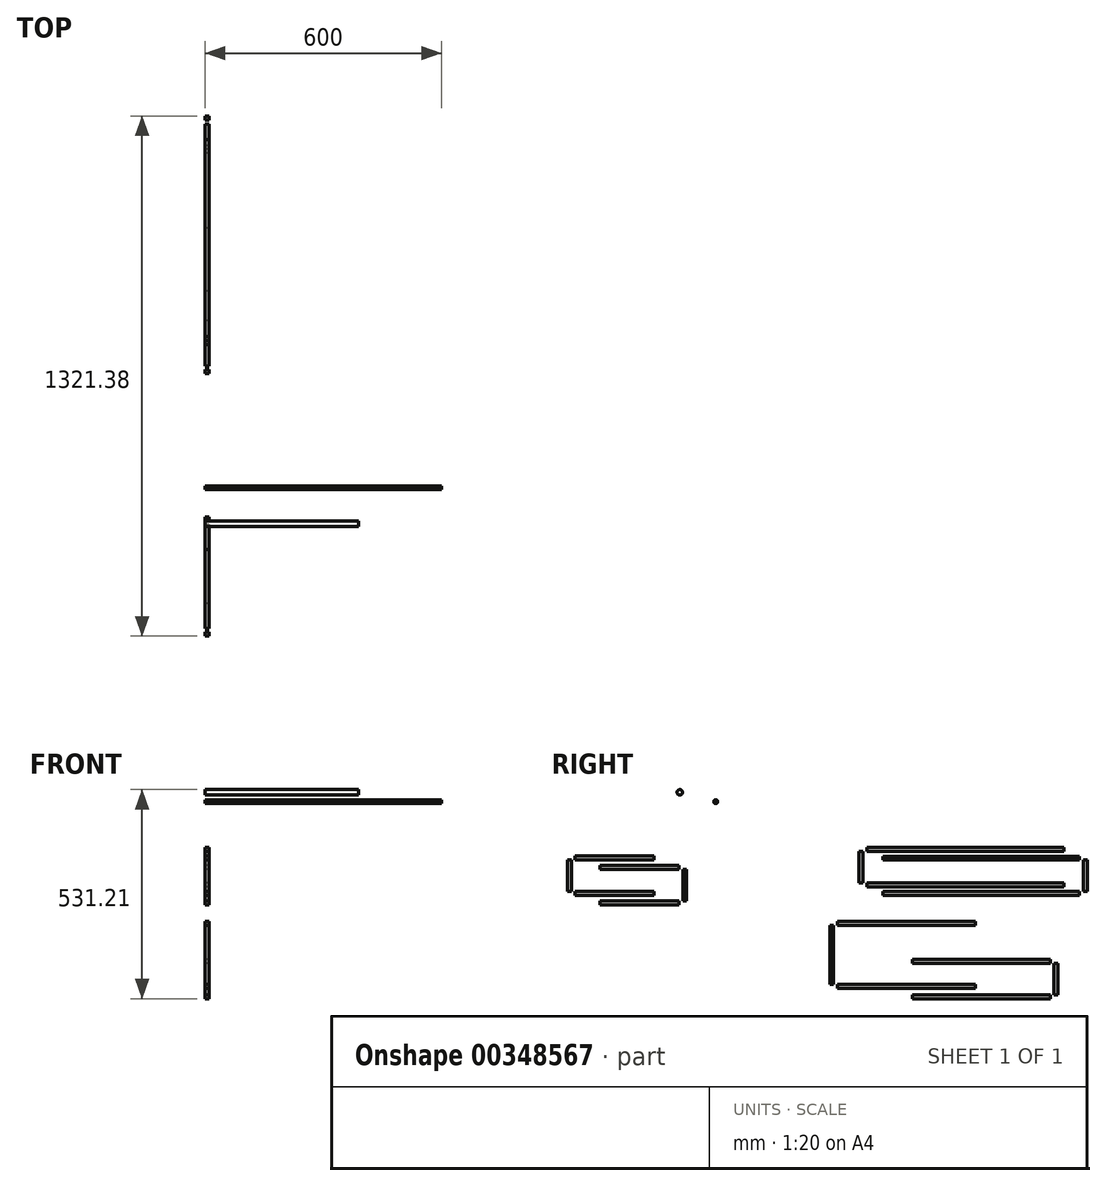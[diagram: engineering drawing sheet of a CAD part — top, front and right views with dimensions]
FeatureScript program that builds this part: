
annotation { "Feature Type Name" : "Feature", "Feature Type Description" : "" }
export const myFeature = defineFeature(function(context is Context, id is Id, definition is map)
    precondition{}
    {
        {
            var Q0;
            Q0=qCreatedBy(makeId("Right.planeOp"),FACE);
            var sketch = newSketch(context, id + "F0", { "sketchPlane" : qUnion([Q0])});
            skLineSegment(sketch, "E0.bottom", {"start": v(-89.52, 73.22) * mm, "end": v(-79.52, 73.22) * mm});
            skLineSegment(sketch, "E0.top", {"start": v(-89.52, -6.78) * mm, "end": v(-79.52, -6.78) * mm});
            skLineSegment(sketch, "E0.left", {"start": v(-89.52, 73.22) * mm, "end": v(-89.52, -6.78) * mm});
            skLineSegment(sketch, "E0.right", {"start": v(-79.52, 73.22) * mm, "end": v(-79.52, -6.78) * mm});
            skLineSegment(sketch, "E1.bottom", {"start": v(-69.52, 73.22) * mm, "end": v(430.48, 73.22) * mm});
            skLineSegment(sketch, "E1.top", {"start": v(-69.52, 83.22) * mm, "end": v(430.48, 83.22) * mm});
            skLineSegment(sketch, "E1.left", {"start": v(-69.52, 73.22) * mm, "end": v(-69.52, 83.22) * mm});
            skLineSegment(sketch, "E1.right", {"start": v(430.48, 73.22) * mm, "end": v(430.48, 83.22) * mm});
            skLineSegment(sketch, "E2.bottom", {"start": v(480.59, 50.91) * mm, "end": v(490.59, 50.91) * mm});
            skLineSegment(sketch, "E2.top", {"start": v(480.59, -29.09) * mm, "end": v(490.59, -29.09) * mm});
            skLineSegment(sketch, "E2.left", {"start": v(480.59, 50.91) * mm, "end": v(480.59, -29.09) * mm});
            skLineSegment(sketch, "E2.right", {"start": v(490.59, 50.91) * mm, "end": v(490.59, -29.09) * mm});
            skLineSegment(sketch, "E3.bottom", {"start": v(470.59, 50.91) * mm, "end": v(-29.41, 50.91) * mm});
            skLineSegment(sketch, "E3.top", {"start": v(470.59, 60.91) * mm, "end": v(-29.41, 60.91) * mm});
            skLineSegment(sketch, "E3.left", {"start": v(470.59, 50.91) * mm, "end": v(470.59, 60.91) * mm});
            skLineSegment(sketch, "E3.right", {"start": v(-29.41, 50.91) * mm, "end": v(-29.41, 60.91) * mm});
            skLineSegment(sketch, "E4.bottom", {"start": v(-69.52, -6.78) * mm, "end": v(430.48, -6.78) * mm});
            skLineSegment(sketch, "E4.top", {"start": v(-69.52, -16.78) * mm, "end": v(430.48, -16.78) * mm});
            skLineSegment(sketch, "E4.left", {"start": v(-69.52, -6.78) * mm, "end": v(-69.52, -16.78) * mm});
            skLineSegment(sketch, "E4.right", {"start": v(430.48, -6.78) * mm, "end": v(430.48, -16.78) * mm});
            skLineSegment(sketch, "E5.bottom", {"start": v(470.59, -29.09) * mm, "end": v(-29.41, -29.09) * mm});
            skLineSegment(sketch, "E5.top", {"start": v(470.59, -39.09) * mm, "end": v(-29.41, -39.09) * mm});
            skLineSegment(sketch, "E5.left", {"start": v(470.59, -29.09) * mm, "end": v(470.59, -39.09) * mm});
            skLineSegment(sketch, "E5.right", {"start": v(-29.41, -29.09) * mm, "end": v(-29.41, -39.09) * mm});
            skSolve(sketch);
        }
        {
            var Q0;
            Q0=qSketchRegion(id+"F0",true);
            extrude(context, id + "F1", {"entities" : qUnion([Q0]), "depth" : 10 * mm});
        }
        {
            var Q0;
            Q0=qCreatedBy(makeId("Right.planeOp"),FACE);
            var sketch = newSketch(context, id + "F2", { "sketchPlane" : qUnion([Q0])});
            skLineSegment(sketch, "E6.bottom", {"start": v(-164.15, -114.36) * mm, "end": v(-154.15, -114.36) * mm});
            skLineSegment(sketch, "E6.top", {"start": v(-164.15, -264.36) * mm, "end": v(-154.15, -264.36) * mm});
            skLineSegment(sketch, "E6.left", {"start": v(-164.15, -114.36) * mm, "end": v(-164.15, -264.36) * mm});
            skLineSegment(sketch, "E6.right", {"start": v(-154.15, -114.36) * mm, "end": v(-154.15, -264.36) * mm});
            skLineSegment(sketch, "E7.bottom", {"start": v(-144.15, -114.36) * mm, "end": v(205.85, -114.36) * mm});
            skLineSegment(sketch, "E7.top", {"start": v(-144.15, -104.36) * mm, "end": v(205.85, -104.36) * mm});
            skLineSegment(sketch, "E7.left", {"start": v(-144.15, -114.36) * mm, "end": v(-144.15, -104.36) * mm});
            skLineSegment(sketch, "E7.right", {"start": v(205.85, -114.36) * mm, "end": v(205.85, -104.36) * mm});
            skLineSegment(sketch, "E8.bottom", {"start": v(405.95, -211.05) * mm, "end": v(415.95, -211.05) * mm});
            skLineSegment(sketch, "E8.top", {"start": v(405.95, -291.05) * mm, "end": v(415.95, -291.05) * mm});
            skLineSegment(sketch, "E8.left", {"start": v(405.95, -211.05) * mm, "end": v(405.95, -291.05) * mm});
            skLineSegment(sketch, "E8.right", {"start": v(415.95, -211.05) * mm, "end": v(415.95, -291.05) * mm});
            skLineSegment(sketch, "E9.bottom", {"start": v(395.95, -211.05) * mm, "end": v(45.95, -211.05) * mm});
            skLineSegment(sketch, "E9.top", {"start": v(395.95, -201.05) * mm, "end": v(45.95, -201.05) * mm});
            skLineSegment(sketch, "E9.left", {"start": v(395.95, -211.05) * mm, "end": v(395.95, -201.05) * mm});
            skLineSegment(sketch, "E9.right", {"start": v(45.95, -211.05) * mm, "end": v(45.95, -201.05) * mm});
            skLineSegment(sketch, "E10.bottom", {"start": v(-144.15, -264.36) * mm, "end": v(205.85, -264.36) * mm});
            skLineSegment(sketch, "E10.top", {"start": v(-144.15, -274.36) * mm, "end": v(205.85, -274.36) * mm});
            skLineSegment(sketch, "E10.left", {"start": v(-144.15, -264.36) * mm, "end": v(-144.15, -274.36) * mm});
            skLineSegment(sketch, "E10.right", {"start": v(205.85, -264.36) * mm, "end": v(205.85, -274.36) * mm});
            skLineSegment(sketch, "E11.bottom", {"start": v(395.95, -291.05) * mm, "end": v(45.95, -291.05) * mm});
            skLineSegment(sketch, "E11.top", {"start": v(395.95, -301.05) * mm, "end": v(45.95, -301.05) * mm});
            skLineSegment(sketch, "E11.left", {"start": v(395.95, -291.05) * mm, "end": v(395.95, -301.05) * mm});
            skLineSegment(sketch, "E11.right", {"start": v(45.95, -291.05) * mm, "end": v(45.95, -301.05) * mm});
            skSolve(sketch);
        }
        {
            var Q0;
            Q0=qSketchRegion(id+"F2",true);
            extrude(context, id + "F3", {"entities" : qUnion([Q0]), "depth" : 10 * mm});
        }
        {
            var Q0;
            Q0=qCreatedBy(makeId("Right.planeOp"),FACE);
            var sketch = newSketch(context, id + "F4", { "sketchPlane" : qUnion([Q0])});
            skLineSegment(sketch, "E12.bottom", {"start": v(-830.8, 51.15) * mm, "end": v(-820.8, 51.15) * mm});
            skLineSegment(sketch, "E12.top", {"start": v(-830.8, -28.85) * mm, "end": v(-820.8, -28.85) * mm});
            skLineSegment(sketch, "E12.left", {"start": v(-830.8, 51.15) * mm, "end": v(-830.8, -28.85) * mm});
            skLineSegment(sketch, "E12.right", {"start": v(-820.8, 51.15) * mm, "end": v(-820.8, -28.85) * mm});
            skLineSegment(sketch, "E13.bottom", {"start": v(-810.8, 51.15) * mm, "end": v(-610.8, 51.15) * mm});
            skLineSegment(sketch, "E13.top", {"start": v(-810.8, 61.15) * mm, "end": v(-610.8, 61.15) * mm});
            skLineSegment(sketch, "E13.left", {"start": v(-810.8, 51.15) * mm, "end": v(-810.8, 61.15) * mm});
            skLineSegment(sketch, "E13.right", {"start": v(-610.8, 51.15) * mm, "end": v(-610.8, 61.15) * mm});
            skLineSegment(sketch, "E14.bottom", {"start": v(-537.58, 27) * mm, "end": v(-527.58, 27) * mm});
            skLineSegment(sketch, "E14.top", {"start": v(-537.58, -53) * mm, "end": v(-527.58, -53) * mm});
            skLineSegment(sketch, "E14.left", {"start": v(-537.58, 27) * mm, "end": v(-537.58, -53) * mm});
            skLineSegment(sketch, "E14.right", {"start": v(-527.58, 27) * mm, "end": v(-527.58, -53) * mm});
            skLineSegment(sketch, "E15.bottom", {"start": v(-547.58, 27) * mm, "end": v(-747.58, 27) * mm});
            skLineSegment(sketch, "E15.top", {"start": v(-547.58, 37) * mm, "end": v(-747.58, 37) * mm});
            skLineSegment(sketch, "E15.left", {"start": v(-547.58, 27) * mm, "end": v(-547.58, 37) * mm});
            skLineSegment(sketch, "E15.right", {"start": v(-747.58, 27) * mm, "end": v(-747.58, 37) * mm});
            skLineSegment(sketch, "E16.bottom", {"start": v(-810.8, -28.85) * mm, "end": v(-610.8, -28.85) * mm});
            skLineSegment(sketch, "E16.top", {"start": v(-810.8, -38.85) * mm, "end": v(-610.8, -38.85) * mm});
            skLineSegment(sketch, "E16.left", {"start": v(-810.8, -28.85) * mm, "end": v(-810.8, -38.85) * mm});
            skLineSegment(sketch, "E16.right", {"start": v(-610.8, -28.85) * mm, "end": v(-610.8, -38.85) * mm});
            skLineSegment(sketch, "E17.bottom", {"start": v(-547.58, -53) * mm, "end": v(-747.58, -53) * mm});
            skLineSegment(sketch, "E17.top", {"start": v(-547.58, -63) * mm, "end": v(-747.58, -63) * mm});
            skLineSegment(sketch, "E17.left", {"start": v(-547.58, -53) * mm, "end": v(-547.58, -63) * mm});
            skLineSegment(sketch, "E17.right", {"start": v(-747.58, -53) * mm, "end": v(-747.58, -63) * mm});
            skSolve(sketch);
        }
        {
            var Q0;
            Q0=qSketchRegion(id+"F4",true);
            extrude(context, id + "F5", {"entities" : qUnion([Q0]), "depth" : 10 * mm});
        }
        {
            var Q0;
            Q0=qCreatedBy(makeId("Right.planeOp"),FACE);
            var sketch = newSketch(context, id + "F6", { "sketchPlane" : qUnion([Q0])});
            skCircle(sketch, "E18", {"center": v(-453.85, 199.49) * mm, "radius": 5 * mm});
            skSolve(sketch);
        }
        {
            var Q0;
            Q0=makeQuery(id+"F6.imprint","IMPRINT",FACE,{"disambiguationData":[TD([[makeQuery(id+"F6.imprint","IMPRINT",EDGE,{"derivedFrom":sQuery(id+"F6.wireOp",EDGE,"E18")}),1.0]])]});
            extrude(context, id + "F7", {"entities" : qUnion([Q0]), "depth" : 600 * mm});
        }
        {
            var Q0;
            Q0=qCreatedBy(makeId("Right.planeOp"),FACE);
            var sketch = newSketch(context, id + "F8", { "sketchPlane" : qUnion([Q0])});
            skCircle(sketch, "E19", {"center": v(-545.08, 223.16) * mm, "radius": 7 * mm});
            skSolve(sketch);
        }
        {
            var Q0;
            Q0=makeQuery(id+"F8.imprint","IMPRINT",FACE,{"disambiguationData":[TD([[makeQuery(id+"F8.imprint","IMPRINT",EDGE,{"derivedFrom":sQuery(id+"F8.wireOp",EDGE,"E19")}),1.0]])]});
            var Q1;
            Q1=sQuery(id+"F8.wireOp",EDGE,"E19");
            extrude(context, id + "F9", {"entities" : qUnion([Q0]), "surfaceEntities" : qUnion([Q1]), "depth" : 390 * mm});
        }
    });
